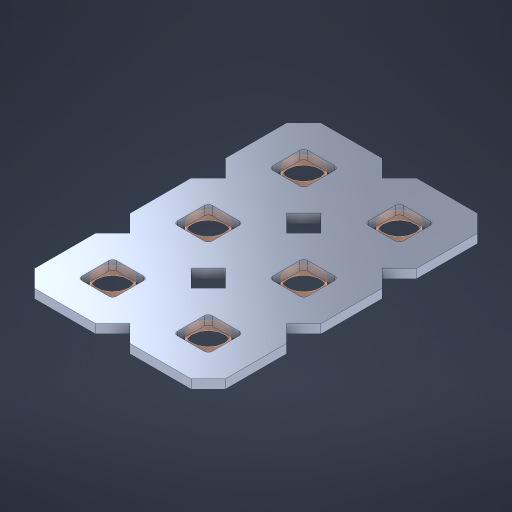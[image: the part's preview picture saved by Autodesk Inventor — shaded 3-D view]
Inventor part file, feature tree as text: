
AUTODESK INVENTOR PART (.ipt)
format: ipt  version: 2023 (Build 270158000, 158)  size: 312,320 bytes
history: native  units: in
note: dims shown in document units (in); Inventor stores cm internally (conversion verified against a paired STEP export)
features: other x7, extrude x5, sketch x2, pattern_linear x1
ambient origin geometry x8: Origin, YZ Plane, XZ Plane, XY Plane, X Axis, Y Axis, Z Axis, Center Point
bodies: Solid1 (feature_tree), Body (feature_tree)
feature tree (15):
  pattern_linear  "Rectangular Pattern1"  Spacing1=0.09in  [1 undecoded]
  sketch  "Sketch1"  dims[d1=0.5in]
  sketch  "Sketch2"  dims[d2=0.182in d3=0.09in d4=0.09in d5=0.09in d6=0.09in d7=0.09in d8=0.09in d9=0.09in d10=0.09in d11=0.02in d13=0.0in d14=0.172in d15=0.0625in d16=0.0in d19=0.5in d22=0.5in]
  other  "Srf1"
  other  "Srf126"
  other  "Srf127"
  other  "Srf268"
  other  "Srf269"
  other  "Srf270"
  other  "Circle"
  extrude  "ExtrusionSrf126"  Depth=0.09in
  extrude  "ExtrusionSrf127"  Depth=0.09in
  extrude  "ExtrusionSrf268"  Depth=0.09in
  extrude  "ExtrusionSrf269"  Depth=0.09in
  extrude  "ExtrusionSrf270"  Depth=0.09in
note: 1 required parameter value undecoded (feature->parameter linkage not recoverable at this tier; creation-order binding heuristic only, values carry confidence <= 0.55)
